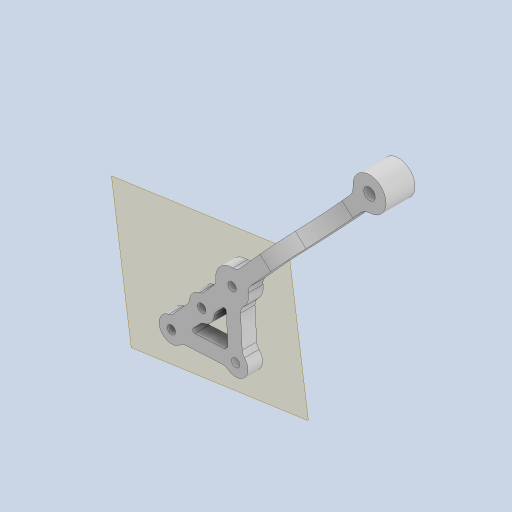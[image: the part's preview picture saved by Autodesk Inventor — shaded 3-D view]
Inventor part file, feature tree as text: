
AUTODESK INVENTOR PART (.ipt)
format: ipt  version: 2023 (Build 270158000, 158)  size: 361,472 bytes
history: native  units: mm
features: extrude x9, sketch x9, projected_geometry x9, other x5, fillet x4, thicken_offset x2, reference x2, plane x1
ambient origin geometry x8: Origin, YZ Plane, XZ Plane, XY Plane, X Axis, Y Axis, Z Axis, Center Point
bodies: Solid1 (feature_tree)
feature tree (41):
  extrude  "Extrusion1"  Depth=3.0mm
  plane  "Work Plane1"
  extrude  "Extrusion2"  Depth=7.0mm
  extrude  "Extrusion3"  Depth=2.0mm
  extrude  "Extrusion4"  Depth=6.0mm
  extrude  "Extrusion5"  Depth=4.0mm
  fillet  "Fillet1"  Radius=12.0mm
  fillet  "Fillet2"  Radius=3.5mm
  thicken_offset  "Thicken1"
  extrude  "Extrusion6"  Depth=3.5mm
  extrude  "Extrusion7"  Depth=5.0mm TaperAngle=0.0deg
  extrude  "Extrusion8"  Depth=4.0mm
  fillet  "Fillet4"  Radius=5.0mm
  extrude  "Extrusion9"  Depth=3.0mm
  fillet  "Fillet5"  Radius=2.0mm
  thicken_offset  "Thicken2"
  sketch  "Sketch1"  dims[d0=8.0mm d1=3.0mm]
  reference  "Reference1"
  sketch  "Sketch2"  dims[d2=7.0mm d3=0.0mm d4=11.0mm]
  reference  "Reference2"
  sketch  "Sketch3"  dims[d5=2.0mm d6=11.0mm]
  projected_geometry  "Projected Loop1"
  projected_geometry  "Projected Loop2"
  sketch  "Sketch4"  dims[d7=2.0mm d8=6.0mm]
  projected_geometry  "Projected Loop3"
  sketch  "Sketch5"  dims[d9=6.0mm d10=4.0mm d11=12.0mm d12=3.5mm]
  projected_geometry  "Projected Loop4"
  projected_geometry  "Projected Loop5"
  sketch  "Sketch6"  dims[d13=3.5mm d14=0.0mm d15=8.0mm]
  projected_geometry  "Projected Loop6"
  sketch  "Sketch7"  dims[d16=3.5mm d17=5.0mm d18=0.0mm]
  projected_geometry  "Projected Loop7"
  sketch  "Sketch8"  dims[d19=5.0mm d20=4.0mm d21=5.0mm d22=0.0mm]
  projected_geometry  "Projected Loop8"
  sketch  "Sketch9"  dims[d23=3.5mm d24=0.0mm d28=3.0mm d29=2.0mm d30=1.5mm d31=1.5mm d32=2.0mm d33=3.5mm d34=0.0mm d35=11.0mm d36=2.0mm d37=6.0mm d38=3.5mm d39=3.5mm d40=3.5mm d41=0.0mm d42=6.0mm d43=3.5mm d44=0.0mm d46=0.5mm d47=8.0mm d48=10.0mm d49=0.0mm d50=2.0mm d51=0.1mm d52=0.05mm]
  projected_geometry  "Projected Loop9"
  parser-record x1  (decoder bookkeeping rows leaked as tree rows — omitted from the tree; the rows remain in map.json)
  other  "leg_1.iam"
  other  "leg_link_1:1"
  other  "reducer_1:2"
  other  "tendon_wh_2:1"
note: 1 file-system path scrubbed to <path> (originals preserved in map.json)
